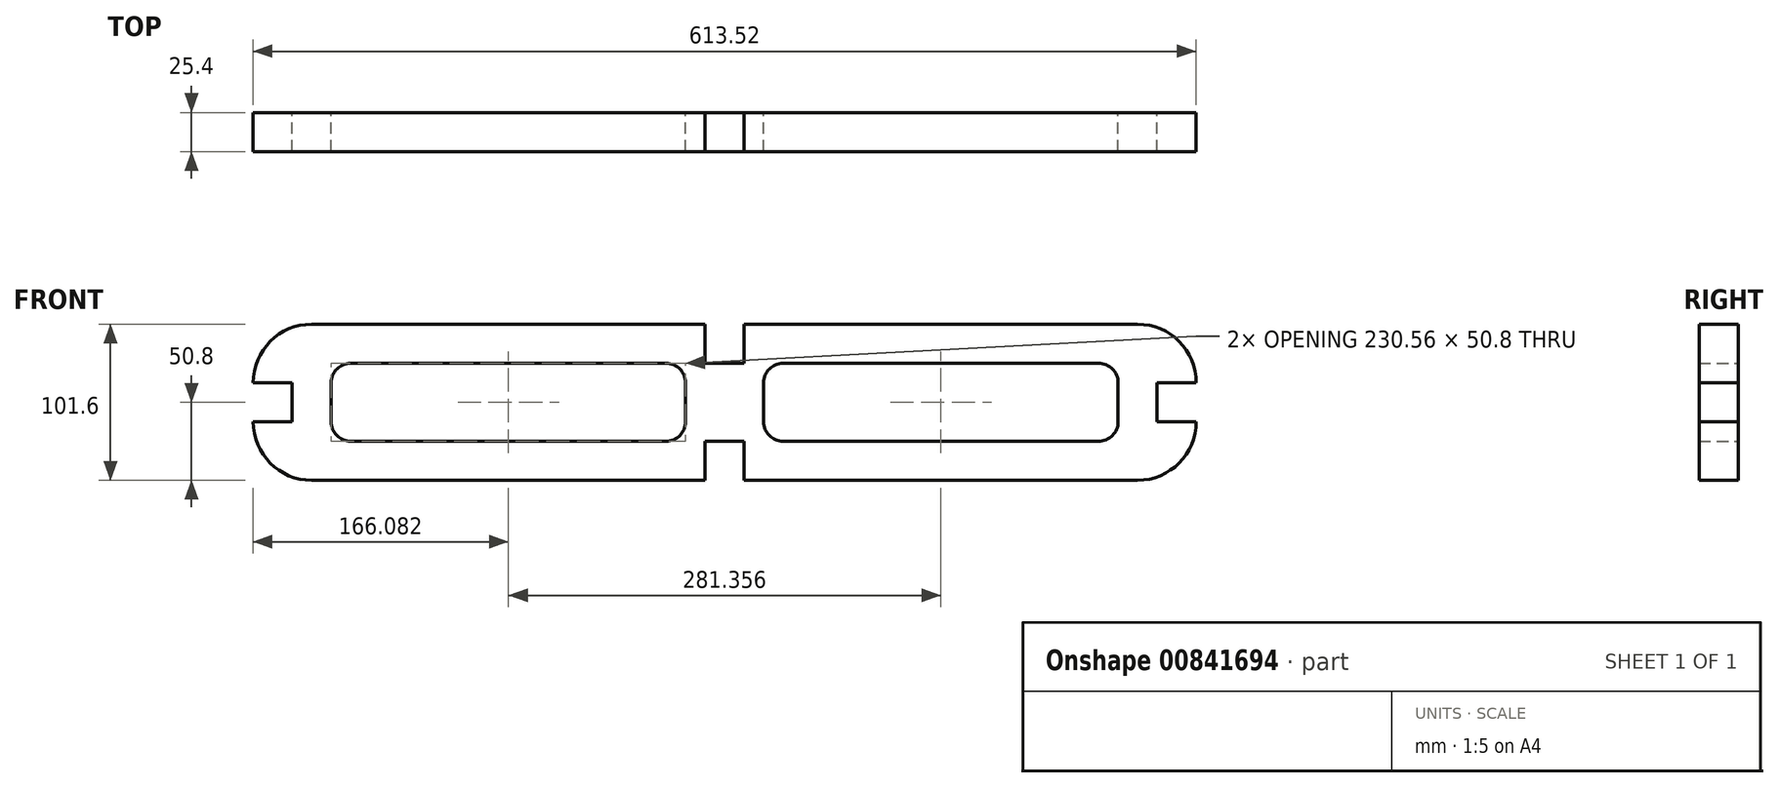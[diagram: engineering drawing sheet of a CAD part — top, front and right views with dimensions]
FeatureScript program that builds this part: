
annotation { "Feature Type Name" : "Feature", "Feature Type Description" : "" }
export const myFeature = defineFeature(function(context is Context, id is Id, definition is map)
    precondition{}
    {
        {
            var Q0;
            Q0=qCreatedBy(makeId("Front.planeOp"),FACE);
            var sketch = newSketch(context, id + "F0", { "sketchPlane" : qUnion([Q0])});
            skLineSegment(sketch, "E0", {"start": v(0, 0) * mm, "end": v(-281.36, 0) * mm, "construction": true});
            skLineSegment(sketch, "E1", {"start": v(0, 0) * mm, "end": v(0, 50.8) * mm, "construction": true});
            skLineSegment(sketch, "E2", {"start": v(0, 0) * mm, "end": v(0, -50.8) * mm, "construction": true});
            skLineSegment(sketch, "E3", {"start": v(-281.36, 12.7) * mm, "end": v(-281.36, -12.7) * mm});
            skLineSegment(sketch, "E4", {"start": v(-281.36, 12.7) * mm, "end": v(-306.76, 12.7) * mm});
            skLineSegment(sketch, "E5", {"start": v(-281.36, -12.7) * mm, "end": v(-306.76, -12.7) * mm});
            skLineSegment(sketch, "E6", {"start": v(0, 50.8) * mm, "end": v(-268.66, 50.8) * mm});
            skLineSegment(sketch, "E7", {"start": v(-268.66, 50.8) * mm, "end": v(-268.66, -50.8) * mm, "construction": true});
            skLineSegment(sketch, "E8", {"start": v(-268.66, -50.8) * mm, "end": v(0, -50.8) * mm});
            skArc(sketch, "E9", {"start": v(-268.66, 50.8) * mm, "mid": v(-295.6, 39.64) * mm, "end": v(-306.76, 12.7) * mm});
            skLineSegment(sketch, "E10", {"start": v(-306.76, 12.7) * mm, "end": v(-306.76, -12.7) * mm, "construction": true});
            skArc(sketch, "E11", {"start": v(-306.76, -12.7) * mm, "mid": v(-295.6, -39.64) * mm, "end": v(-268.66, -50.8) * mm});
            skLineSegment(sketch, "E12.bottom", {"start": v(-243.26, -25.4) * mm, "end": v(-38.1, -25.4) * mm});
            skLineSegment(sketch, "E12.top", {"start": v(-243.26, 25.4) * mm, "end": v(-38.1, 25.4) * mm});
            skLineSegment(sketch, "E12.left", {"start": v(-255.96, -12.7) * mm, "end": v(-255.96, 12.7) * mm});
            skLineSegment(sketch, "E12.right", {"start": v(-25.4, -12.7) * mm, "end": v(-25.4, 12.7) * mm});
            skPoint(sketch, "E13.visualSharp", {"position": v(-255.96, 25.4) * mm});
            skArc(sketch, "E13.filletArc", {"start": v(-243.26, 25.4) * mm, "mid": v(-252.24, 21.68) * mm, "end": v(-255.96, 12.7) * mm});
            skPoint(sketch, "E14.visualSharp", {"position": v(-255.96, -25.4) * mm});
            skArc(sketch, "E14.filletArc", {"start": v(-255.96, -12.7) * mm, "mid": v(-252.24, -21.68) * mm, "end": v(-243.26, -25.4) * mm});
            skPoint(sketch, "E15.visualSharp", {"position": v(-25.4, 25.4) * mm});
            skArc(sketch, "E15.filletArc", {"start": v(-25.4, 12.7) * mm, "mid": v(-29.12, 21.68) * mm, "end": v(-38.1, 25.4) * mm});
            skPoint(sketch, "E16.visualSharp", {"position": v(-25.4, -25.4) * mm});
            skArc(sketch, "E16.filletArc", {"start": v(-38.1, -25.4) * mm, "mid": v(-29.12, -21.68) * mm, "end": v(-25.4, -12.7) * mm});
            skLineSegment(sketch, "E17.MirrorCS", {"start": v(0, 50.8) * mm, "end": v(268.66, 50.8) * mm});
            skArc(sketch, "E18.MirrorCS", {"start": v(268.66, 50.8) * mm, "mid": v(295.6, 39.64) * mm, "end": v(306.76, 12.7) * mm});
            skLineSegment(sketch, "E19.MirrorCS", {"start": v(281.36, 12.7) * mm, "end": v(306.76, 12.7) * mm});
            skLineSegment(sketch, "E20.MirrorCS", {"start": v(281.36, 12.7) * mm, "end": v(281.36, -12.7) * mm});
            skArc(sketch, "E21.MirrorCS", {"start": v(306.76, -12.7) * mm, "mid": v(295.6, -39.64) * mm, "end": v(268.66, -50.8) * mm});
            skLineSegment(sketch, "E22.MirrorCS", {"start": v(268.66, -50.8) * mm, "end": v(0, -50.8) * mm});
            skLineSegment(sketch, "E23.MirrorCS", {"start": v(243.26, -25.4) * mm, "end": v(38.1, -25.4) * mm});
            skArc(sketch, "E24.MirrorCS", {"start": v(255.96, -12.7) * mm, "mid": v(252.24, -21.68) * mm, "end": v(243.26, -25.4) * mm});
            skLineSegment(sketch, "E25.MirrorCS", {"start": v(255.96, -12.7) * mm, "end": v(255.96, 12.7) * mm});
            skArc(sketch, "E26.MirrorCS", {"start": v(243.26, 25.4) * mm, "mid": v(252.24, 21.68) * mm, "end": v(255.96, 12.7) * mm});
            skLineSegment(sketch, "E27.MirrorCS", {"start": v(243.26, 25.4) * mm, "end": v(38.1, 25.4) * mm});
            skArc(sketch, "E28.MirrorCS", {"start": v(25.4, 12.7) * mm, "mid": v(29.12, 21.68) * mm, "end": v(38.1, 25.4) * mm});
            skLineSegment(sketch, "E29.MirrorCS", {"start": v(25.4, -12.7) * mm, "end": v(25.4, 12.7) * mm});
            skArc(sketch, "E30.MirrorCS", {"start": v(38.1, -25.4) * mm, "mid": v(29.12, -21.68) * mm, "end": v(25.4, -12.7) * mm});
            skLineSegment(sketch, "E31.MirrorCS", {"start": v(281.36, -12.7) * mm, "end": v(306.76, -12.7) * mm});
            skSolve(sketch);
        }
        {
            var Q0;
            Q0 = qSketchRegion(id + "F0", true);
            extrude(context, id + "F1", {"entities" : qUnion([Q0]), "depth" : 25.4 * mm, "offsetDistance" : 25.4 * mm});
        }
        {
            var Q0;
            Q0=makeQuery(id+"F1.opExtrude","CAP_FACE",FACE,{"disambiguationData":[OSD([sQuery(id+"F0.wireOp",EDGE,"E3"),sQuery(id+"F0.wireOp",EDGE,"E4"),sQuery(id+"F0.wireOp",EDGE,"E5"),sQuery(id+"F0.wireOp",EDGE,"E6"),sQuery(id+"F0.wireOp",EDGE,"E8"),sQuery(id+"F0.wireOp",EDGE,"E9"),sQuery(id+"F0.wireOp",EDGE,"E11"),sQuery(id+"F0.wireOp",EDGE,"E12.bottom"),sQuery(id+"F0.wireOp",EDGE,"E12.top"),sQuery(id+"F0.wireOp",EDGE,"E12.left"),sQuery(id+"F0.wireOp",EDGE,"E12.right"),sQuery(id+"F0.wireOp",EDGE,"E13.filletArc"),sQuery(id+"F0.wireOp",EDGE,"E14.filletArc"),sQuery(id+"F0.wireOp",EDGE,"E15.filletArc"),sQuery(id+"F0.wireOp",EDGE,"E16.filletArc"),sQuery(id+"F0.wireOp",EDGE,"E17.MirrorCS"),sQuery(id+"F0.wireOp",EDGE,"E18.MirrorCS"),sQuery(id+"F0.wireOp",EDGE,"E19.MirrorCS"),sQuery(id+"F0.wireOp",EDGE,"E20.MirrorCS"),sQuery(id+"F0.wireOp",EDGE,"E21.MirrorCS"),sQuery(id+"F0.wireOp",EDGE,"E22.MirrorCS"),sQuery(id+"F0.wireOp",EDGE,"E23.MirrorCS"),sQuery(id+"F0.wireOp",EDGE,"E24.MirrorCS"),sQuery(id+"F0.wireOp",EDGE,"E25.MirrorCS"),sQuery(id+"F0.wireOp",EDGE,"E26.MirrorCS"),sQuery(id+"F0.wireOp",EDGE,"E27.MirrorCS"),sQuery(id+"F0.wireOp",EDGE,"E28.MirrorCS"),sQuery(id+"F0.wireOp",EDGE,"E29.MirrorCS"),sQuery(id+"F0.wireOp",EDGE,"E30.MirrorCS"),sQuery(id+"F0.wireOp",EDGE,"E31.MirrorCS")])],"isStart":false});
            var sketch = newSketch(context, id + "F2", { "sketchPlane" : qUnion([Q0])});
            skLineSegment(sketch, "E32", {"start": v(0, 0) * mm, "end": v(0, 25.4) * mm, "construction": true});
            skLineSegment(sketch, "E33", {"start": v(0, 0) * mm, "end": v(0, -25.4) * mm, "construction": true});
            skLineSegment(sketch, "E34.bottom", {"start": v(-12.7, 50.8) * mm, "end": v(12.7, 50.8) * mm});
            skLineSegment(sketch, "E34.top", {"start": v(-12.7, 25.4) * mm, "end": v(12.7, 25.4) * mm});
            skLineSegment(sketch, "E34.left", {"start": v(-12.7, 50.8) * mm, "end": v(-12.7, 25.4) * mm});
            skLineSegment(sketch, "E34.right", {"start": v(12.7, 50.8) * mm, "end": v(12.7, 25.4) * mm});
            skLineSegment(sketch, "E35.bottom", {"start": v(-12.7, -50.8) * mm, "end": v(12.7, -50.8) * mm});
            skLineSegment(sketch, "E35.top", {"start": v(-12.7, -25.4) * mm, "end": v(12.7, -25.4) * mm});
            skLineSegment(sketch, "E35.left", {"start": v(-12.7, -50.8) * mm, "end": v(-12.7, -25.4) * mm});
            skLineSegment(sketch, "E35.right", {"start": v(12.7, -50.8) * mm, "end": v(12.7, -25.4) * mm});
            skSolve(sketch);
        }
        {
            var Q0;
            Q0 = qSketchRegion(id + "F2", true);
            extrude(context, id + "F3", {"entities" : qUnion([Q0]), "operationType" : NewBodyOperationType.REMOVE, "oppositeDirection" : true, "depth" : 25.4 * mm, "offsetDistance" : 25.4 * mm});
        }
    });
